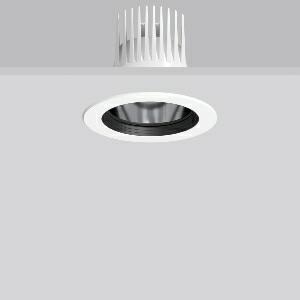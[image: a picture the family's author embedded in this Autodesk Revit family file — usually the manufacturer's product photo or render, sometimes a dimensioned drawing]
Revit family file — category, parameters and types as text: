
# Revit family: heledon_maxi_e_901787_002_2_814d
name_source: partatom
category: Lighting Fixtures
units: mm (PartAtom-declared; Revit-internal decimal feet)

## family parameters
Cut with Voids When Loaded = No
Host = Face
Light Source = No
Part Type = Normal
Room Calculation Point = No
Round Connector Dimension = Use Diameter
Shared = No

## types (1)
- HELEDON maxi E (1 x LED Modul 927 bakery, 3300 lm, 2700)
    Apparent Load = 33 VA
    Approval mark = CE
    CIE Flux Codes = 96 100 100 100 100
    Color Rendering = 90
    Color Temperature = 2700
    Default Elevation = 1800 mm
    Description = Series: HELEDON maxi
Round recessed downlight. Housing: die-cast aluminium, powder-coated. Black plastic ring and recessed LED to prevent glare from the side. Optical assembly with reflector made of MIRO-Silver with 98% total light reflection for outstanding efficiency - can be changed without tools. Special LED for illumination of pastries included. Suitable for Recessed ceiling mounting. Installation without tools thanks to spring fastening system. Including separate LED converter with connecting cable 600 mm.High quality converter without flickering and stroboscopic effect. Through-wiring box (5 pole) available as accessory. The following accessories can be mounted without use of tools: interchangeable lenses, decorative glasses, honeycomb louvre, clear and frosted diffusers, white interchangeable plastic ring. 
Colour: traffic white, matt (RAL 9016)
Diameter: 162 mm
Height: 3 mm
Cut-out diameter: 152 mm
Recess height: 200 mm
Luminaire: recess height: 135 mm
Lamp: LED
Socket: without socket
Colour temperature: bakery
Colour rendering index (CRI): 97
System power: 33 W
Rated luminous flux: 3300 lm
Luminous efficiency: 100 lm/W
Control gear: Regulated power supply
Protection class: II
Type of protection: IP 20
    Height = 0 mm  [stored 0 ft]
    Lamp = 1 x LED Modul 927 bakery
    Lamp Light Flux = 3300 lm
    Lamp count = 1
    Length = 162 mm
    Lifetime = 50000 h
    Luminous efficacy = 100 lm/W
    Manufacturer = RZB
    ModVariant = No
    Model = 901787.002.2
    Mounting Place = Ceiling
    Mounting Type = Recessed
    Number of Poles = 1
    OnlyDefault = Yes
    Power Factor = 1
    Product Name = HELEDON maxi E
    Product group = Recessed downlights
    ProductGroupID = 402
    Protection Class = Protection class II
    Protection Degree = IP 20
    RLX_Detail_Level = 1
    RLX_Emergency_Light_Flux = 0 lm
    RLX_Emergency_Type = 0
    RLX_Emergency_Type_DB = No
    RlxData = <blob elided: 119213 chars, md5=19f5070c>
    Socket = socket
    Standby Power = 0 W
    System Light Flux = 3300 lm
    System Power = 33 W
    Type Comments = Product without accessories
    Type Image = 901662.002.jpg
    URL = http://relux.com
    VarID = ---
    Voltage = 230 V
    Voltage Range = 220-240 V
    Weight = 0.00 kg
    Width = 0 mm  [stored 0 ft]

note: [stored X ft] marks values corroborated as IEEE doubles in the binary element streams (Revit-internal decimal feet)

## geometry (parser evidence)
native form markers: Blend x4, Sweep x10
no freeform markers — native parametric forms only
